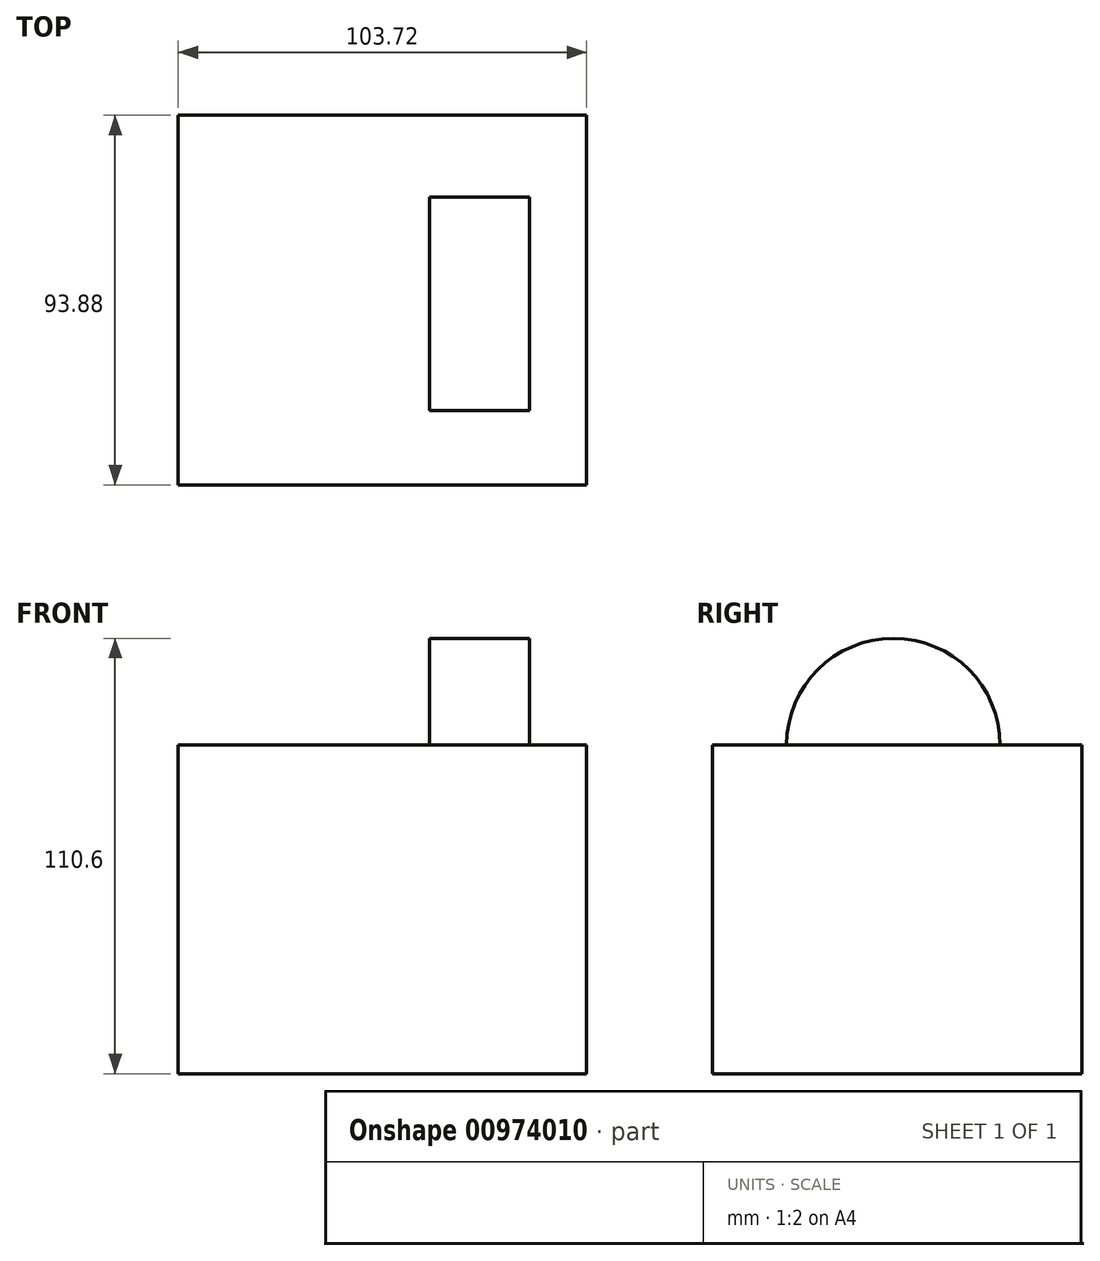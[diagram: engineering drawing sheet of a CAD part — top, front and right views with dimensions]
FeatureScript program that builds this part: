
annotation { "Feature Type Name" : "Feature", "Feature Type Description" : "" }
export const myFeature = defineFeature(function(context is Context, id is Id, definition is map)
    precondition{}
    {
        {
            var Q0;
            Q0=qCreatedBy(makeId("Top.planeOp"),FACE);
            var sketch = newSketch(context, id + "F0", { "sketchPlane" : qUnion([Q0])});
            skLineSegment(sketch, "E0.bottom", {"start": v(-47.47, 41.51) * mm, "end": v(56.25, 41.51) * mm});
            skLineSegment(sketch, "E0.top", {"start": v(-47.47, -52.37) * mm, "end": v(56.25, -52.37) * mm});
            skLineSegment(sketch, "E0.left", {"start": v(-47.47, 41.51) * mm, "end": v(-47.47, -52.37) * mm});
            skLineSegment(sketch, "E0.right", {"start": v(56.25, 41.51) * mm, "end": v(56.25, -52.37) * mm});
            skSolve(sketch);
        }
        {
            var Q0;
            Q0=makeQuery(id+"F0.imprint","IMPRINT",FACE,{"disambiguationData":[TD([[makeQuery(id+"F0.imprint","IMPRINT",EDGE,{"derivedFrom":sQuery(id+"F0.wireOp",EDGE,"E0.bottom")}),-1.0]])]});
            extrude(context, id + "F1", {"entities" : qUnion([Q0]), "depth" : 83.48 * mm, "offsetDistance" : 25.4 * mm});
        }
        {
            var Q0;
            Q0=makeQuery(id+"F1.opExtrude","CAP_FACE",FACE,{"disambiguationData":[OSD([sQuery(id+"F0.wireOp",EDGE,"E0.bottom"),sQuery(id+"F0.wireOp",EDGE,"E0.top"),sQuery(id+"F0.wireOp",EDGE,"E0.left"),sQuery(id+"F0.wireOp",EDGE,"E0.right")])],"isStart":false});
            var sketch = newSketch(context, id + "F2", { "sketchPlane" : qUnion([Q0])});
            skLineSegment(sketch, "E1.bottom", {"start": v(-26.65, 41.51) * mm, "end": v(4.4, 41.51) * mm});
            skLineSegment(sketch, "E1.top", {"start": v(-26.65, -52.37) * mm, "end": v(4.4, -52.37) * mm});
            skLineSegment(sketch, "E1.left", {"start": v(-26.65, 41.51) * mm, "end": v(-26.65, -52.37) * mm});
            skLineSegment(sketch, "E1.right", {"start": v(4.4, 41.51) * mm, "end": v(4.4, -52.37) * mm});
            skLineSegment(sketch, "E2.bottom", {"start": v(22.07, 41.51) * mm, "end": v(41.77, 41.51) * mm});
            skLineSegment(sketch, "E2.top", {"start": v(22.07, -52.37) * mm, "end": v(41.77, -52.37) * mm});
            skLineSegment(sketch, "E2.left", {"start": v(22.07, 41.51) * mm, "end": v(22.07, -52.37) * mm});
            skLineSegment(sketch, "E2.right", {"start": v(41.77, 41.51) * mm, "end": v(41.77, -52.37) * mm});
            skLineSegment(sketch, "E3.bottom", {"start": v(56.25, 20.7) * mm, "end": v(41.77, 20.7) * mm});
            skLineSegment(sketch, "E3.top", {"start": v(56.25, -33.55) * mm, "end": v(41.77, -33.55) * mm});
            skLineSegment(sketch, "E3.left", {"start": v(56.25, 20.7) * mm, "end": v(56.25, -33.55) * mm});
            skLineSegment(sketch, "E3.right", {"start": v(41.77, 20.7) * mm, "end": v(41.77, -33.55) * mm});
            skLineSegment(sketch, "E4.bottom", {"start": v(41.77, 20.7) * mm, "end": v(41.77, 20.7) * mm});
            skLineSegment(sketch, "E4.top", {"start": v(41.77, -33.55) * mm, "end": v(41.77, -33.55) * mm});
            skLineSegment(sketch, "E5.bottom", {"start": v(-26.65, -14.29) * mm, "end": v(5.1, -14.29) * mm});
            skLineSegment(sketch, "E5.top", {"start": v(-26.65, 3.2) * mm, "end": v(5.1, 3.2) * mm});
            skLineSegment(sketch, "E5.left", {"start": v(-26.65, -14.29) * mm, "end": v(-26.65, 3.2) * mm});
            skLineSegment(sketch, "E5.right", {"start": v(5.1, -14.29) * mm, "end": v(5.1, 3.2) * mm});
            skLineSegment(sketch, "E6.bottom", {"start": v(5.1, -14.29) * mm, "end": v(5.1, -14.29) * mm});
            skLineSegment(sketch, "E6.top", {"start": v(5.1, 3.2) * mm, "end": v(5.1, 3.2) * mm});
            skSolve(sketch);
        }
        {
            var Q0;
            Q0=sQuery(id+"F2.wireOp",EDGE,"E3.right");
            extrude(context, id + "F3", {"bodyType" : ToolBodyType.SURFACE, "surfaceEntities" : qUnion([Q0]), "depth" : 54.6 * mm, "offsetDistance" : 25.4 * mm});
        }
        {
            var Q0;
            Q0=makeQuery(id+"F3.opExtrude","SWEPT_FACE",FACE,{"disambiguationData":[OSD([sQuery(id+"F2.wireOp",EDGE,"E3.right")])]});
            var sketch = newSketch(context, id + "F4", { "sketchPlane" : qUnion([Q0])});
            skLineSegment(sketch, "E7", {"start": v(6.43, 138.07) * mm, "end": v(6.43, 83.48) * mm});
            skLineSegment(sketch, "E8", {"start": v(6.43, 110.77) * mm, "end": v(-20.7, 110.77) * mm});
            skLineSegment(sketch, "E9", {"start": v(6.43, 110.77) * mm, "end": v(33.55, 110.77) * mm});
            skArc(sketch, "E10", {"start": v(33.55, 83.48) * mm, "mid": v(6.43, 110.6) * mm, "end": v(-20.7, 83.48) * mm});
            skSolve(sketch);
        }
        {
            var Q0;
            {var subQ0=sQuery(id+"F4.wireOp",EDGE,"E7");var subQ1=makeQuery(id+"F3.opExtrude","CAP_EDGE",EDGE,{"disambiguationData":[OSD([sQuery(id+"F2.wireOp",EDGE,"E3.right")])],"isStart":true});var subQ2=makeQuery(id+"F4.imprint","INTERSECT",VERTEX,{"derivedFrom":[subQ1,subQ0]});Q0=makeQuery(id+"F4.imprint","IMPRINT",FACE,{"disambiguationData":[TD([[makeQuery(id+"F4.imprint","IMPRINT",EDGE,{"disambiguationData":[TD([[subQ2,1.0]])],"derivedFrom":subQ0}),-1.0]])]});}
            var Q1;
            {var subQ0=sQuery(id+"F4.wireOp",EDGE,"E7");var subQ1=makeQuery(id+"F3.opExtrude","CAP_EDGE",EDGE,{"disambiguationData":[OSD([sQuery(id+"F2.wireOp",EDGE,"E3.right")])],"isStart":true});var subQ2=makeQuery(id+"F4.imprint","INTERSECT",VERTEX,{"derivedFrom":[subQ1,subQ0]});Q1=makeQuery(id+"F4.imprint","IMPRINT",FACE,{"disambiguationData":[TD([[makeQuery(id+"F4.imprint","IMPRINT",EDGE,{"disambiguationData":[TD([[subQ2,1.0]])],"derivedFrom":subQ0}),1.0]])]});}
            extrude(context, id + "F5", {"entities" : qUnion([Q0, Q1]), "depth" : 25.4 * mm, "offsetDistance" : 25.4 * mm});
        }
        {
            var Q0;
            Q0=makeQuery(id+"F3.opExtrude","SWEPT_BODY",BODY,{"disambiguationData":[OSD([sQuery(id+"F2.wireOp",EDGE,"E3.right")])]});
            deleteBodies(context, id + "F6", {"entities" : qUnion([Q0])});
        }
    });
